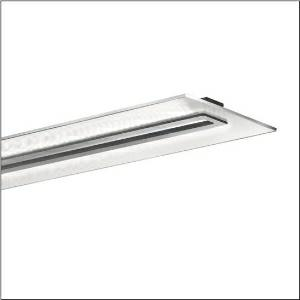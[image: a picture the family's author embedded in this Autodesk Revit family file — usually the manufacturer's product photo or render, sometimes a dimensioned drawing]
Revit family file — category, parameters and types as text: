
# Revit family: vega_11_5mn238dlc
name_source: partatom
category: Lighting Fixtures
units: mm (PartAtom-declared; Revit-internal decimal feet)

## family parameters
Cut with Voids When Loaded = No
Host = Face
Light Source = No
Part Type = Normal
Room Calculation Point = No
Round Connector Dimension = Use Diameter
Shared = No

## types (1)
- --- (1 x LED 4000K / CRI = 80 (unbekannt), 4300 lm, 4000K)
    Apparent Load = 31 VA
    CIE Flux Codes = 61 86 97 62 100
    Color Rendering = 80
    Color Temperature = 4000K
    Default Elevation = 1800 mm
    Description = Vega 11, office luminaire, primary light control with prismatic reflector, of PMMA, transparent prismatic structure, CAT 2 (L<= 1500cd/m²), light emission: direct/indirect distribution, primary light characteristic: symmetric, installation type: suspended mounting, surface-mounted, LED, rated luminous flux: 4.300lm, luminous efficacy: 139lm/W, light colour: 840, colour temperature: 4000K, control gear: DALI, with terminal, 3+2-pole, max. 2.5mm², mains connection: 230V, AC, 50Hz, connection cable inclusive, cable length: 1,5m, rated input power: 31W, luminaire housing, rectangular, rounded, of aluminium section, anodised, metallic grey (RAL 9006), length: 1.250mm, width: 350mm, height: 43mm, luminaire housing, lower part, of aluminium section, anodised, metallic grey (RAL 9006), of PC, grey, protection rating (complete): IP20, insulation class (complete): insulation class I (protective earthing), certification: CE, standard: EN 50419, packaging unit: 1 piece
    Height = 40 mm  [stored 0.131234 ft]
    Lamp = 1 x LED 4000K / CRI >= 80 (unbekannt)
    Lamp Light Flux = 4300 lm
    Lamp count = 1
    Length = 1250 mm
    Luminous efficacy = 139 lm/W
    Manufacturer = Siteco
    ModVariant = No
    Model = 5MN238DLC
    Mounting Place = Ceiling
    Mounting Type = Pendant
    Number of Poles = 1
    OnlyDefault = Yes
    Power Factor = 1
    Product Name = Vega 11
    Product group = office luminaire | ceiling pendant
    ProductGroupID = 903
    Protection Class = Protection class I
    Protection Degree = IP 20
    RLX_Detail_Level = 1
    RLX_Emergency_Light_Flux = 0 lm
    RLX_Emergency_Type = 0
    RLX_Emergency_Type_DB = No
    RlxData = <blob elided: 62813 chars, md5=b1a36864>
    Socket = socket
    Standby Power = 0 W
    System Light Flux = 4300 lm
    System Power = 31 W
    Type Comments = factory setting: luminous flux: 100 % | dim-lin: 254 | 231 mA
    Type Image = l_1004807.jpg
    URL = http://relux.com
    VarID = @adj_196943
    Voltage = 0 V
    Weight = 0.00 kg
    Width = 350 mm

note: [stored X ft] marks values corroborated as IEEE doubles in the binary element streams (Revit-internal decimal feet)

## geometry (parser evidence)
native form markers: Blend x4, Sweep x11
no freeform markers — native parametric forms only
